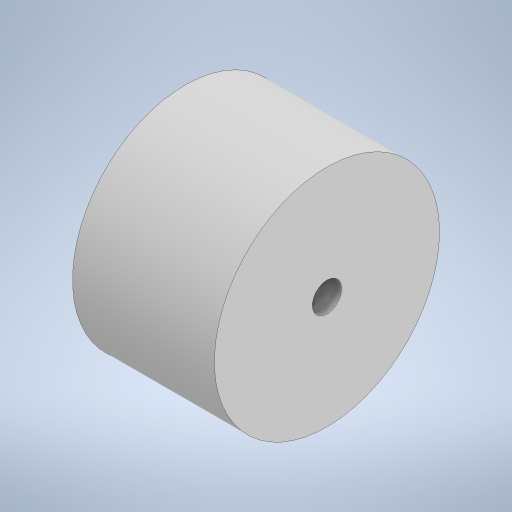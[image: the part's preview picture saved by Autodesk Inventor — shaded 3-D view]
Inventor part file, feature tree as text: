
AUTODESK INVENTOR PART (.ipt)
format: ipt  version: 2023 (Build 270158000, 158)  size: 208,896 bytes
history: native  units: mm
features: extrude x2, sketch x2, other x1
ambient origin geometry x8: Origin, YZ Plane, XZ Plane, XY Plane, X Axis, Y Axis, Z Axis, Center Point
bodies: Body1 (feature_tree)
feature tree (5):
  other  "Bryła1"
  extrude  "Wyciągnięcie proste1"  Depth=30.0mm
  extrude  "Wyciągnięcie proste2"  Depth=3.0mm
  sketch  "Szkic1"
  sketch  "Szkic2"
